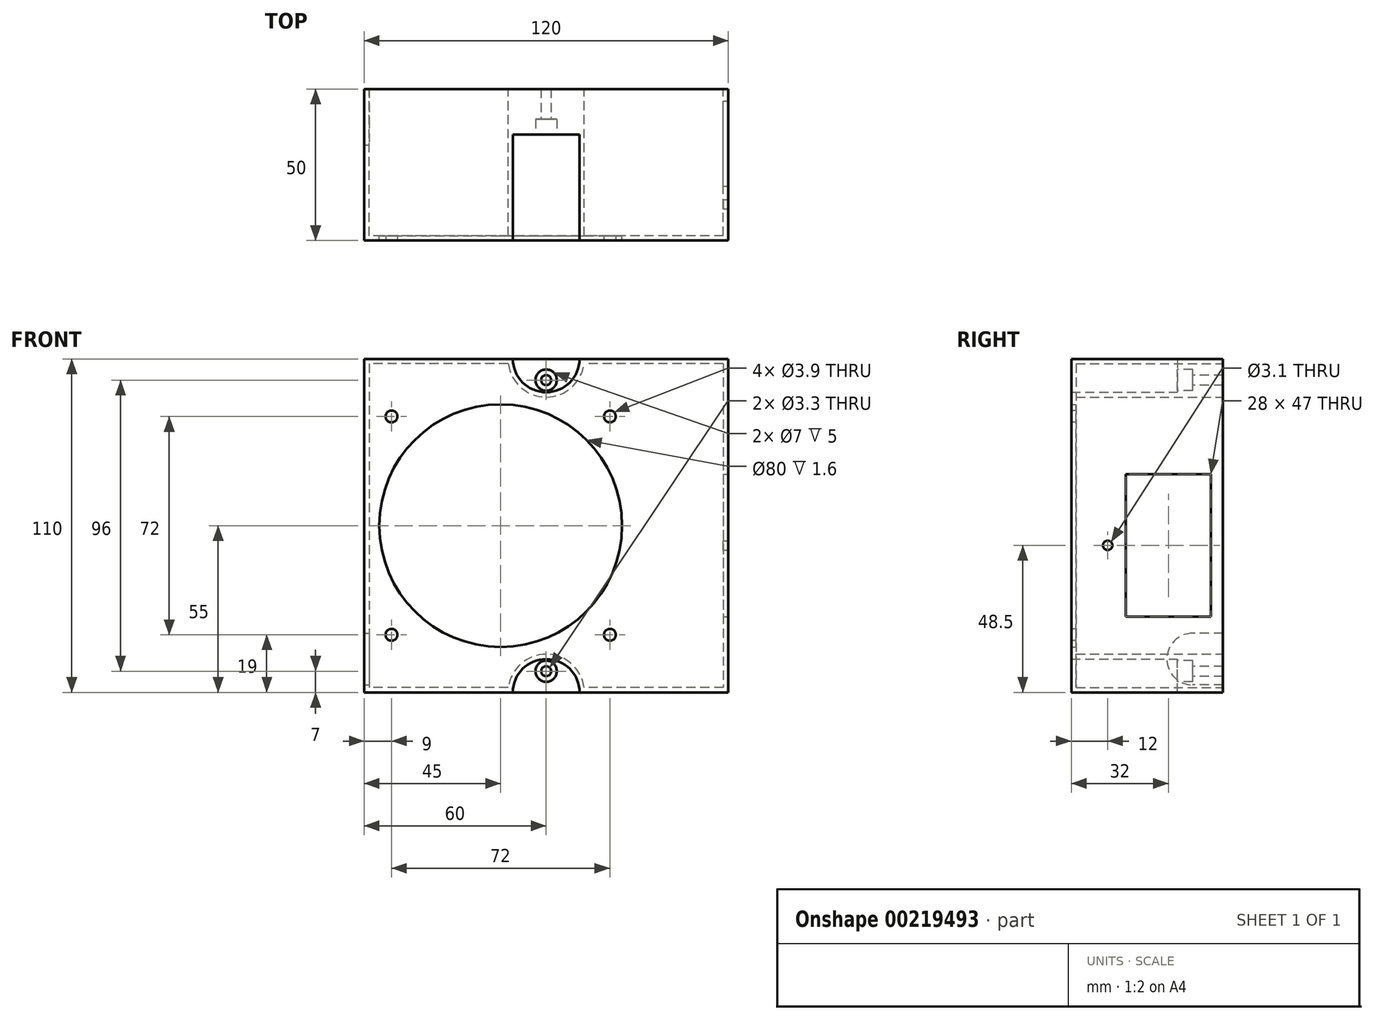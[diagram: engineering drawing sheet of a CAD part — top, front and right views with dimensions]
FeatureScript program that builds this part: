
annotation { "Feature Type Name" : "Feature", "Feature Type Description" : "" }
export const myFeature = defineFeature(function(context is Context, id is Id, definition is map)
    precondition{}
    {
        {
            var Q0;
            Q0=qCreatedBy(makeId("Front.planeOp"),FACE);
            var sketch = newSketch(context, id + "F0", { "sketchPlane" : qUnion([Q0])});
            skLineSegment(sketch, "E0.bottom", {"start": v(60, 55) * mm, "end": v(11, 55) * mm});
            skLineSegment(sketch, "E0.top", {"start": v(60, -55) * mm, "end": v(11, -55) * mm});
            skLineSegment(sketch, "E0.left", {"start": v(60, 55) * mm, "end": v(60, -55) * mm});
            skLineSegment(sketch, "E0.right", {"start": v(-60, 55) * mm, "end": v(-60, -55) * mm});
            skPoint(sketch, "E0.middle", {"position": v(0, 0) * mm});
            skArc(sketch, "E1", {"start": v(11, -55) * mm, "mid": v(0, -44) * mm, "end": v(-11, -55) * mm});
            skLineSegment(sketch, "E2.trimOffspring", {"start": v(-11, -55) * mm, "end": v(-60, -55) * mm});
            skArc(sketch, "E3.MirrorCS", {"start": v(11, 55) * mm, "mid": v(0, 44) * mm, "end": v(-11, 55) * mm});
            skLineSegment(sketch, "E4.trimOffspring", {"start": v(-11, 55) * mm, "end": v(-60, 55) * mm});
            skSolve(sketch);
        }
        {
            var Q0;
            Q0 = qSketchRegion(id + "F0", true);
            extrude(context, id + "F1", {"entities" : qUnion([Q0]), "depth" : 50 * mm});
        }
        {
            var Q0;
            Q0=makeQuery(id+"F1.opExtrude","CAP_FACE",FACE,{"disambiguationData":[OSD([sQuery(id+"F0.wireOp",EDGE,"E0.bottom"),sQuery(id+"F0.wireOp",EDGE,"E0.top"),sQuery(id+"F0.wireOp",EDGE,"E0.left"),sQuery(id+"F0.wireOp",EDGE,"E0.right"),sQuery(id+"F0.wireOp",EDGE,"E1"),sQuery(id+"F0.wireOp",EDGE,"E2.trimOffspring"),sQuery(id+"F0.wireOp",EDGE,"E3.MirrorCS"),sQuery(id+"F0.wireOp",EDGE,"E4.trimOffspring")])],"isStart":true});
            shell(context, id + "F2", {"entities" : qUnion([Q0]), "thickness" : 1.6 * mm});
        }
        {
            var Q0;
            Q0=qCreatedBy(makeId("Front.planeOp"),FACE);
            var sketch = newSketch(context, id + "F3", { "sketchPlane" : qUnion([Q0])});
            skPoint(sketch, "E5", {"position": v(-15, 0) * mm});
            skSolve(sketch);
        }
        {
            var Q0;
            Q0=sQuery(id+"F3.wireOp",VERTEX,"E5");
            var Q1;
            Q1=makeQuery(id+"F1.opExtrude","SWEPT_BODY",BODY,{"disambiguationData":[OSD([sQuery(id+"F0.wireOp",EDGE,"E0.bottom"),sQuery(id+"F0.wireOp",EDGE,"E0.top"),sQuery(id+"F0.wireOp",EDGE,"E0.left"),sQuery(id+"F0.wireOp",EDGE,"E0.right"),sQuery(id+"F0.wireOp",EDGE,"E1"),sQuery(id+"F0.wireOp",EDGE,"E2.trimOffspring"),sQuery(id+"F0.wireOp",EDGE,"E3.MirrorCS"),sQuery(id+"F0.wireOp",EDGE,"E4.trimOffspring")])]});
            hole(context, id + "F4", {"style" : HoleStyle.SIMPLE, "endStyle" : HoleEndStyle.THROUGH, "oppositeDirection" : true, "holeDiameter" : 80 * mm, "locations" : qUnion([Q0]), "scope" : qUnion([Q1]), "isTappedThrough" : true});
        }
        {
            var Q0;
            Q0=makeQuery(id+"F1.opExtrude","SWEPT_FACE",FACE,{"disambiguationData":[OSD([sQuery(id+"F0.wireOp",EDGE,"E0.left")])]});
            var sketch = newSketch(context, id + "F5", { "sketchPlane" : qUnion([Q0])});
            skLineSegment(sketch, "E6.bottom", {"start": v(-32, 17) * mm, "end": v(-4, 17) * mm});
            skLineSegment(sketch, "E6.top", {"start": v(-32, -30) * mm, "end": v(-4, -30) * mm});
            skLineSegment(sketch, "E6.left", {"start": v(-32, 17) * mm, "end": v(-32, -30) * mm});
            skLineSegment(sketch, "E6.right", {"start": v(-4, 17) * mm, "end": v(-4, -30) * mm});
            skSolve(sketch);
        }
        {
            var Q0;
            Q0 = qSketchRegion(id + "F5", true);
            extrude(context, id + "F6", {"entities" : qUnion([Q0]), "operationType" : NewBodyOperationType.REMOVE, "oppositeDirection" : true, "depth" : 5.1 * mm});
        }
        {
            var Q0;
            Q0=makeQuery(id+"F1.opExtrude","SWEPT_FACE",FACE,{"disambiguationData":[OSD([sQuery(id+"F0.wireOp",EDGE,"E0.left")])]});
            var sketch = newSketch(context, id + "F7", { "sketchPlane" : qUnion([Q0])});
            skPoint(sketch, "E7", {"position": v(-10, -44) * mm});
            skCircle(sketch, "E8", {"center": v(-10, -44) * mm, "radius": 8.5 * mm});
            skLineSegment(sketch, "E9.bottom", {"start": v(0, -35.5) * mm, "end": v(-10.02, -35.5) * mm});
            skLineSegment(sketch, "E9.top", {"start": v(0, -52.5) * mm, "end": v(-10.02, -52.5) * mm});
            skLineSegment(sketch, "E9.left", {"start": v(0, -35.5) * mm, "end": v(0, -52.5) * mm});
            skLineSegment(sketch, "E9.right", {"start": v(-10.02, -35.5) * mm, "end": v(-10.02, -52.5) * mm});
            skSolve(sketch);
        }
        {
            var Q0;
            {var subQ0=sQuery(id+"F7.wireOp",EDGE,"E9.right");Q0=makeQuery(id+"F7.imprint","IMPRINT",FACE,{"disambiguationData":[TD([[makeQuery(id+"F7.imprint","IMPRINT",EDGE,{"derivedFrom":subQ0}),-1.0]])]});}
            var Q1;
            {var subQ5=sQuery(id+"F7.wireOp",EDGE,"E9.right");Q1=makeQuery(id+"F7.imprint","IMPRINT",FACE,{"disambiguationData":[TD([[makeQuery(id+"F7.imprint","IMPRINT",EDGE,{"derivedFrom":subQ5}),1.0]])]});}
            var Q2;
            {var subQ5=sQuery(id+"F7.wireOp",EDGE,"E9.left");Q2=makeQuery(id+"F7.imprint","IMPRINT",FACE,{"disambiguationData":[TD([[makeQuery(id+"F7.imprint","IMPRINT",EDGE,{"derivedFrom":subQ5}),-1.0]])]});}
            extrude(context, id + "F8", {"entities" : qUnion([Q0, Q1, Q2]), "operationType" : NewBodyOperationType.REMOVE, "oppositeDirection" : true, "depth" : 147 * mm, "hasSecondDirection" : true, "secondDirectionOppositeDirection" : true, "secondDirectionDepth" : 94.2 * mm});
        }
        {
            var Q0;
            Q0=qCreatedBy(makeId("Front.planeOp"),FACE);
            var sketch = newSketch(context, id + "F9", { "sketchPlane" : qUnion([Q0])});
            skPoint(sketch, "E10.middle", {"position": v(0, 0) * mm});
            skArc(sketch, "E11", {"start": v(11, -55) * mm, "mid": v(0, -44) * mm, "end": v(-11, -55) * mm});
            skLineSegment(sketch, "E12", {"start": v(-11, -55) * mm, "end": v(11, -55) * mm});
            skArc(sketch, "E13.MirrorCS", {"start": v(11, 55) * mm, "mid": v(0, 44) * mm, "end": v(-11, 55) * mm});
            skLineSegment(sketch, "E14.MirrorCS", {"start": v(-11, 55) * mm, "end": v(11, 55) * mm});
            skSolve(sketch);
        }
        {
            var Q0;
            Q0 = qSketchRegion(id + "F9", true);
            extrude(context, id + "F10", {"entities" : qUnion([Q0]), "operationType" : NewBodyOperationType.ADD, "depth" : 15 * mm});
        }
        {
            var Q0;
            Q0=makeQuery(id+"F10.opExtrude","CAP_FACE",FACE,{"disambiguationData":[OSD([sQuery(id+"F9.wireOp",EDGE,"E11"),sQuery(id+"F9.wireOp",EDGE,"E12")])],"isStart":false});
            var sketch = newSketch(context, id + "F11", { "sketchPlane" : qUnion([Q0])});
            skPoint(sketch, "E15", {"position": v(0, -48) * mm});
            skPoint(sketch, "E16.MirrorP", {"position": v(0, 48) * mm});
            skSolve(sketch);
        }
        {
            var Q0;
            Q0=sQuery(id+"F11.wireOp",VERTEX,"E16.MirrorP");
            var Q1;
            Q1=sQuery(id+"F11.wireOp",VERTEX,"E15");
            var Q2;
            Q2=makeQuery(id+"F1.opExtrude","SWEPT_BODY",BODY,{"disambiguationData":[OSD([sQuery(id+"F0.wireOp",EDGE,"E0.bottom"),sQuery(id+"F0.wireOp",EDGE,"E0.top"),sQuery(id+"F0.wireOp",EDGE,"E0.left"),sQuery(id+"F0.wireOp",EDGE,"E0.right"),sQuery(id+"F0.wireOp",EDGE,"E1"),sQuery(id+"F0.wireOp",EDGE,"E2.trimOffspring"),sQuery(id+"F0.wireOp",EDGE,"E3.MirrorCS"),sQuery(id+"F0.wireOp",EDGE,"E4.trimOffspring")])]});
            hole(context, id + "F12", {"style" : HoleStyle.C_BORE, "endStyle" : HoleEndStyle.THROUGH, "holeDiameter" : 3.3 * mm, "cBoreDiameter" : 7 * mm, "cBoreDepth" : 5 * mm, "locations" : qUnion([Q0, Q1]), "scope" : qUnion([Q2]), "isTappedThrough" : true});
        }
        {
            var Q0;
            Q0=makeQuery(id+"F1.opExtrude","SWEPT_FACE",FACE,{"disambiguationData":[OSD([sQuery(id+"F0.wireOp",EDGE,"E0.left")])]});
            var sketch = newSketch(context, id + "F13", { "sketchPlane" : qUnion([Q0])});
            skPoint(sketch, "E17", {"position": v(-38, -6.5) * mm});
            skLineSegment(sketch, "E18", {"start": v(-18, 17) * mm, "end": v(-18, -30) * mm, "construction": true});
            skPoint(sketch, "E19.MirrorP", {"position": v(2, -6.5) * mm});
            skSolve(sketch);
        }
        {
            var Q0;
            Q0=sQuery(id+"F13.wireOp",VERTEX,"E17");
            var Q1;
            Q1=makeQuery(id+"F1.opExtrude","SWEPT_BODY",BODY,{"disambiguationData":[OSD([sQuery(id+"F0.wireOp",EDGE,"E0.bottom"),sQuery(id+"F0.wireOp",EDGE,"E0.top"),sQuery(id+"F0.wireOp",EDGE,"E0.left"),sQuery(id+"F0.wireOp",EDGE,"E0.right"),sQuery(id+"F0.wireOp",EDGE,"E1"),sQuery(id+"F0.wireOp",EDGE,"E2.trimOffspring"),sQuery(id+"F0.wireOp",EDGE,"E3.MirrorCS"),sQuery(id+"F0.wireOp",EDGE,"E4.trimOffspring")])]});
            hole(context, id + "F14", {"style" : HoleStyle.SIMPLE, "endStyle" : HoleEndStyle.BLIND, "holeDiameter" : 3.1 * mm, "holeDepth" : 12 * mm, "locations" : qUnion([Q0]), "scope" : qUnion([Q1])});
        }
        {
            var Q0;
            Q0=makeQuery(id+"F1.opExtrude","CAP_FACE",FACE,{"disambiguationData":[OSD([sQuery(id+"F0.wireOp",EDGE,"E0.bottom"),sQuery(id+"F0.wireOp",EDGE,"E0.top"),sQuery(id+"F0.wireOp",EDGE,"E0.left"),sQuery(id+"F0.wireOp",EDGE,"E0.right"),sQuery(id+"F0.wireOp",EDGE,"E1"),sQuery(id+"F0.wireOp",EDGE,"E2.trimOffspring"),sQuery(id+"F0.wireOp",EDGE,"E3.MirrorCS"),sQuery(id+"F0.wireOp",EDGE,"E4.trimOffspring")])],"isStart":false});
            var sketch = newSketch(context, id + "F15", { "sketchPlane" : qUnion([Q0])});
            skLineSegment(sketch, "E20.bottom", {"start": v(-55, 40) * mm, "end": v(25, 40) * mm, "construction": true});
            skLineSegment(sketch, "E20.top", {"start": v(-55, -40) * mm, "end": v(25, -40) * mm, "construction": true});
            skLineSegment(sketch, "E20.left", {"start": v(-55, 40) * mm, "end": v(-55, -40) * mm, "construction": true});
            skLineSegment(sketch, "E20.right", {"start": v(25, 40) * mm, "end": v(25, -40) * mm, "construction": true});
            skPoint(sketch, "E20.middle", {"position": v(-15, 0) * mm});
            skLineSegment(sketch, "E21.bottom", {"start": v(-51, 36) * mm, "end": v(21, 36) * mm, "construction": true});
            skLineSegment(sketch, "E21.top", {"start": v(-51, -36) * mm, "end": v(21, -36) * mm, "construction": true});
            skLineSegment(sketch, "E21.left", {"start": v(-51, 36) * mm, "end": v(-51, -36) * mm, "construction": true});
            skLineSegment(sketch, "E21.right", {"start": v(21, 36) * mm, "end": v(21, -36) * mm, "construction": true});
            skSolve(sketch);
        }
        {
            var Q0;
            Q0=sQuery(id+"F15.wireOp",VERTEX,"E21.left.start");
            var Q1;
            Q1=sQuery(id+"F15.wireOp",VERTEX,"E21.bottom.end");
            var Q2;
            Q2=sQuery(id+"F15.wireOp",VERTEX,"E21.top.end");
            var Q3;
            Q3=sQuery(id+"F15.wireOp",VERTEX,"E21.top.start");
            var Q4;
            Q4=makeQuery(id+"F1.opExtrude","SWEPT_BODY",BODY,{"disambiguationData":[OSD([sQuery(id+"F0.wireOp",EDGE,"E0.bottom"),sQuery(id+"F0.wireOp",EDGE,"E0.top"),sQuery(id+"F0.wireOp",EDGE,"E0.left"),sQuery(id+"F0.wireOp",EDGE,"E0.right"),sQuery(id+"F0.wireOp",EDGE,"E1"),sQuery(id+"F0.wireOp",EDGE,"E2.trimOffspring"),sQuery(id+"F0.wireOp",EDGE,"E3.MirrorCS"),sQuery(id+"F0.wireOp",EDGE,"E4.trimOffspring")])]});
            hole(context, id + "F16", {"style" : HoleStyle.SIMPLE, "endStyle" : HoleEndStyle.BLIND, "holeDiameter" : 3.9 * mm, "holeDepth" : 12 * mm, "locations" : qUnion([Q0, Q1, Q2, Q3]), "scope" : qUnion([Q4])});
        }
    });
